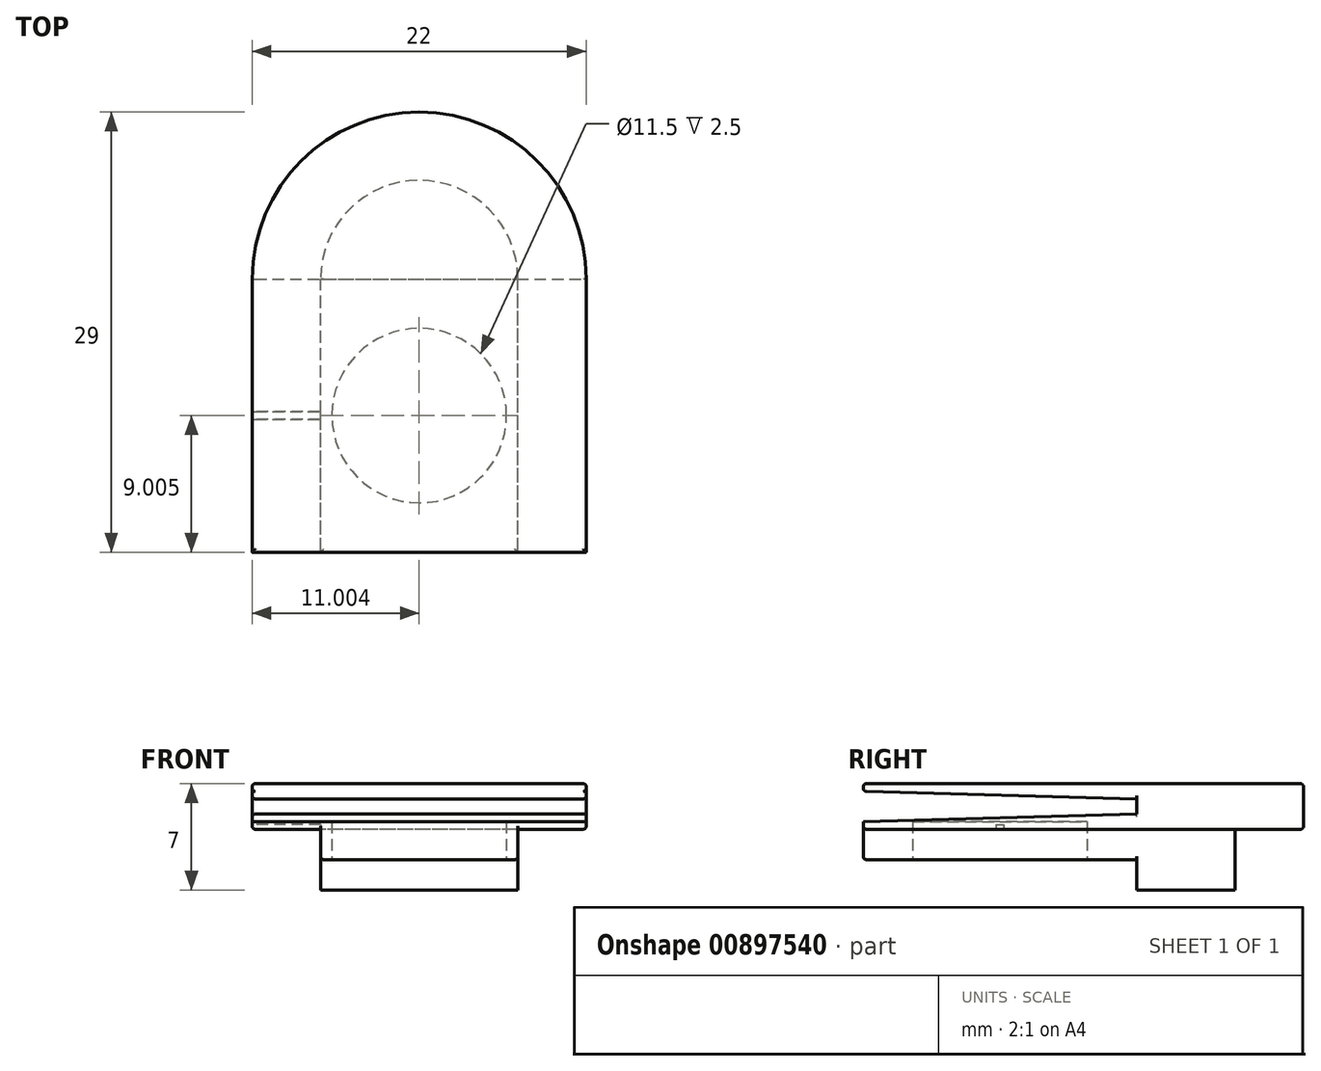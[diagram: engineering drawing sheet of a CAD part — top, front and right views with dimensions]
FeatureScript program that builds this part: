
annotation { "Feature Type Name" : "Feature", "Feature Type Description" : "" }
export const myFeature = defineFeature(function(context is Context, id is Id, definition is map)
    precondition{}
    {
        {
            var Q0;
            Q0=qCreatedBy(makeId("Top.planeOp"),FACE);
            var sketch = newSketch(context, id + "F0", { "sketchPlane" : qUnion([Q0])});
            skArc(sketch, "E0", {"start": v(-33.64, 30.56) * mm, "mid": v(-40.14, 37.06) * mm, "end": v(-46.64, 30.56) * mm});
            skLineSegment(sketch, "E1", {"start": v(-40.14, 30.56) * mm, "end": v(-33.64, 30.56) * mm});
            skLineSegment(sketch, "E2", {"start": v(-33.64, 30.56) * mm, "end": v(-46.64, 30.56) * mm});
            skLineSegment(sketch, "E3", {"start": v(-40.14, 30.56) * mm, "end": v(-40.14, 37.06) * mm, "construction": true});
            skSolve(sketch);
        }
        {
            var Q0;
            Q0 = qSketchRegion(id + "F0", true);
            extrude(context, id + "F1", {"entities" : qUnion([Q0]), "depth" : 13 * mm, "offsetDistance" : 25 * mm});
        }
        {
            var Q0;
            Q0=makeQuery(id+"F1.opExtrude","SWEPT_FACE",FACE,{"disambiguationData":[OSD([sQuery(id+"F0.wireOp",EDGE,"E2")])]});
            var sketch = newSketch(context, id + "F2", { "sketchPlane" : qUnion([Q0])});
            skLineSegment(sketch, "E4.bottom", {"start": v(-46.64, 13) * mm, "end": v(-33.64, 13) * mm});
            skLineSegment(sketch, "E4.top", {"start": v(-46.64, 10) * mm, "end": v(-33.64, 10) * mm});
            skLineSegment(sketch, "E4.left", {"start": v(-46.64, 13) * mm, "end": v(-46.64, 10) * mm});
            skLineSegment(sketch, "E4.right", {"start": v(-33.64, 13) * mm, "end": v(-33.64, 10) * mm});
            skSolve(sketch);
        }
        {
            var Q0;
            Q0 = qSketchRegion(id + "F2", true);
            extrude(context, id + "F3", {"entities" : qUnion([Q0]), "depth" : 18 * mm, "offsetDistance" : 25 * mm});
        }
        {
            var Q0;
            Q0=makeQuery(id+"F3.boolean.opBoolean","MERGE",FACE,{"derivedFrom":[makeQuery(id+"F1.opExtrude","CAP_FACE",FACE,{"disambiguationData":[OSD([sQuery(id+"F0.wireOp",EDGE,"E0"),sQuery(id+"F0.wireOp",EDGE,"E2")])],"isStart":false}),makeQuery(id+"F3.opExtrude","SWEPT_FACE",FACE,{"disambiguationData":[OSD([sQuery(id+"F2.wireOp",EDGE,"E4.bottom")])]})]});
            var sketch = newSketch(context, id + "F4", { "sketchPlane" : qUnion([Q0])});
            skArc(sketch, "E5.0", {"start": v(-29.14, 30.56) * mm, "mid": v(-40.14, 41.56) * mm, "end": v(-51.14, 30.56) * mm});
            skLineSegment(sketch, "E6", {"start": v(-51.14, 30.56) * mm, "end": v(-46.64, 30.56) * mm});
            skLineSegment(sketch, "E7", {"start": v(-29.14, 30.56) * mm, "end": v(-33.64, 30.56) * mm});
            skArc(sketch, "E8.0", {"start": v(-33.64, 30.56) * mm, "mid": v(-40.14, 37.06) * mm, "end": v(-46.64, 30.56) * mm});
            skSolve(sketch);
        }
        {
            var Q0;
            Q0 = qSketchRegion(id + "F4", true);
            extrude(context, id + "F5", {"entities" : qUnion([Q0]), "oppositeDirection" : true, "depth" : 3 * mm, "offsetDistance" : 25 * mm});
        }
        {
            var Q0;
            Q0=makeQuery(id+"F5.opExtrude","SWEPT_FACE",FACE,{"disambiguationData":[OSD([sQuery(id+"F4.wireOp",EDGE,"E6")])]});
            var sketch = newSketch(context, id + "F6", { "sketchPlane" : qUnion([Q0])});
            skLineSegment(sketch, "E9.bottom", {"start": v(-51.14, 10) * mm, "end": v(-46.64, 10) * mm});
            skLineSegment(sketch, "E9.top", {"start": v(-51.14, 13) * mm, "end": v(-46.64, 13) * mm});
            skLineSegment(sketch, "E9.left", {"start": v(-51.14, 10) * mm, "end": v(-51.14, 13) * mm});
            skLineSegment(sketch, "E9.right", {"start": v(-46.64, 10) * mm, "end": v(-46.64, 13) * mm});
            skSolve(sketch);
        }
        {
            var Q0;
            Q0 = qSketchRegion(id + "F6", true);
            extrude(context, id + "F7", {"entities" : qUnion([Q0]), "depth" : 18 * mm, "offsetDistance" : 25 * mm});
        }
        {
            var Q0;
            Q0=makeQuery(id+"F5.opExtrude","SWEPT_FACE",FACE,{"disambiguationData":[OSD([sQuery(id+"F4.wireOp",EDGE,"E7")])]});
            var sketch = newSketch(context, id + "F8", { "sketchPlane" : qUnion([Q0])});
            skLineSegment(sketch, "E10.bottom", {"start": v(-33.64, 13) * mm, "end": v(-29.14, 13) * mm});
            skLineSegment(sketch, "E10.top", {"start": v(-33.64, 10) * mm, "end": v(-29.14, 10) * mm});
            skLineSegment(sketch, "E10.left", {"start": v(-33.64, 13) * mm, "end": v(-33.64, 10) * mm});
            skLineSegment(sketch, "E10.right", {"start": v(-29.14, 13) * mm, "end": v(-29.14, 10) * mm});
            skSolve(sketch);
        }
        {
            var Q0;
            Q0 = qSketchRegion(id + "F8", true);
            extrude(context, id + "F9", {"entities" : qUnion([Q0]), "depth" : 18 * mm, "offsetDistance" : 25 * mm});
        }
        {
            var Q0;
            Q0=makeQuery(id+"F7.opExtrude","SWEPT_FACE",FACE,{"disambiguationData":[OSD([sQuery(id+"F6.wireOp",EDGE,"E9.bottom")])]});
            var sketch = newSketch(context, id + "F10", { "sketchPlane" : qUnion([Q0])});
            skLineSegment(sketch, "E11.bottom", {"start": v(-46.64, -21.31) * mm, "end": v(-51.14, -21.31) * mm});
            skLineSegment(sketch, "E11.top", {"start": v(-46.64, -21.81) * mm, "end": v(-51.14, -21.81) * mm});
            skLineSegment(sketch, "E11.left", {"start": v(-46.64, -21.31) * mm, "end": v(-46.64, -21.81) * mm});
            skLineSegment(sketch, "E11.right", {"start": v(-51.14, -21.31) * mm, "end": v(-51.14, -21.81) * mm});
            skPoint(sketch, "E11.middle", {"position": v(-48.89, -21.56) * mm});
            skPoint(sketch, "E11.middle.positionSnap0", {"position": v(-51.14, -21.56) * mm});
            skPoint(sketch, "E11.middle.positionSnap1", {"position": v(-48.89, -30.56) * mm});
            skPoint(sketch, "E11.centerSnap0", {"position": v(-51.14, -21.56) * mm});
            skPoint(sketch, "E11.centerSnap1", {"position": v(-48.89, -30.56) * mm});
            skSolve(sketch);
        }
        {
            var Q0;
            Q0 = qSketchRegion(id + "F10", true);
            extrude(context, id + "F11", {"entities" : qUnion([Q0]), "depth" : 0.5 * mm, "offsetDistance" : 25 * mm});
        }
        {
            var Q0;
            Q0=makeQuery(id+"F11.opExtrude","CAP_FACE",FACE,{"disambiguationData":[OSD([sQuery(id+"F10.wireOp",EDGE,"E11.bottom"),sQuery(id+"F10.wireOp",EDGE,"E11.top"),sQuery(id+"F10.wireOp",EDGE,"E11.left"),sQuery(id+"F10.wireOp",EDGE,"E11.right")])],"isStart":false});
            var sketch = newSketch(context, id + "F12", { "sketchPlane" : qUnion([Q0])});
            skLineSegment(sketch, "E12.bottom", {"start": v(-51.14, -21.81) * mm, "end": v(-46.64, -21.81) * mm});
            skLineSegment(sketch, "E12.top", {"start": v(-51.14, -21.31) * mm, "end": v(-46.64, -21.31) * mm});
            skLineSegment(sketch, "E12.left", {"start": v(-51.14, -21.81) * mm, "end": v(-51.14, -21.31) * mm});
            skLineSegment(sketch, "E12.right", {"start": v(-46.64, -21.81) * mm, "end": v(-46.64, -21.31) * mm});
            skSolve(sketch);
        }
        {
            var Q0;
            Q0 = qSketchRegion(id + "F12", true);
            extrude(context, id + "F13", {"entities" : qUnion([Q0]), "operationType" : NewBodyOperationType.REMOVE, "oppositeDirection" : true, "depth" : 0.8 * mm, "offsetDistance" : 25 * mm});
        }
        {
            var Q0;
            Q0=makeQuery(id+"F1.opExtrude","CAP_FACE",FACE,{"disambiguationData":[OSD([sQuery(id+"F0.wireOp",EDGE,"E0"),sQuery(id+"F0.wireOp",EDGE,"E2")])],"isStart":true});
            var sketch = newSketch(context, id + "F14", { "sketchPlane" : qUnion([Q0])});
            skArc(sketch, "E13", {"start": v(-46.64, -30.56) * mm, "mid": v(-40.14, -37.06) * mm, "end": v(-33.64, -30.56) * mm});
            skLineSegment(sketch, "E14", {"start": v(-46.64, -30.56) * mm, "end": v(-33.64, -30.56) * mm});
            skSolve(sketch);
        }
        {
            var Q0;
            Q0 = qSketchRegion(id + "F14", true);
            extrude(context, id + "F15", {"entities" : qUnion([Q0]), "operationType" : NewBodyOperationType.REMOVE, "oppositeDirection" : true, "depth" : 6 * mm, "offsetDistance" : 25 * mm});
        }
        {
            var Q0;
            Q0=makeQuery(id+"F3.opExtrude","SWEPT_FACE",FACE,{"disambiguationData":[OSD([sQuery(id+"F2.wireOp",EDGE,"E4.top")])]});
            var sketch = newSketch(context, id + "F16", { "sketchPlane" : qUnion([Q0])});
            skLineSegment(sketch, "E15.bottom", {"start": v(-33.64, -30.56) * mm, "end": v(-46.64, -30.56) * mm});
            skLineSegment(sketch, "E15.top", {"start": v(-33.64, -12.56) * mm, "end": v(-46.64, -12.56) * mm});
            skLineSegment(sketch, "E15.left", {"start": v(-33.64, -30.56) * mm, "end": v(-33.64, -12.56) * mm});
            skLineSegment(sketch, "E15.right", {"start": v(-46.64, -30.56) * mm, "end": v(-46.64, -12.56) * mm});
            skSolve(sketch);
        }
        {
            var Q0;
            Q0 = qSketchRegion(id + "F16", true);
            extrude(context, id + "F17", {"entities" : qUnion([Q0]), "operationType" : NewBodyOperationType.ADD, "depth" : 2 * mm, "offsetDistance" : 25 * mm});
        }
        {
            var Q0;
            Q0=makeQuery(id+"F17.opExtrude","CAP_FACE",FACE,{"disambiguationData":[OSD([sQuery(id+"F16.wireOp",EDGE,"E15.bottom"),sQuery(id+"F16.wireOp",EDGE,"E15.top"),sQuery(id+"F16.wireOp",EDGE,"E15.left"),sQuery(id+"F16.wireOp",EDGE,"E15.right")])],"isStart":false});
            var sketch = newSketch(context, id + "F18", { "sketchPlane" : qUnion([Q0])});
            skCircle(sketch, "E16", {"center": v(-40.14, -21.56) * mm, "radius": 5.75 * mm});
            skPoint(sketch, "E16.centerSnap0", {"position": v(-46.64, -21.56) * mm});
            skPoint(sketch, "E16.centerSnap1", {"position": v(-40.14, -30.56) * mm});
            skSolve(sketch);
        }
        {
            var Q0;
            Q0 = qSketchRegion(id + "F18", true);
            extrude(context, id + "F19", {"entities" : qUnion([Q0]), "operationType" : NewBodyOperationType.REMOVE, "oppositeDirection" : true, "depth" : 2.5 * mm, "offsetDistance" : 25 * mm});
        }
        {
            var Q0;
            Q0=makeQuery(id+"F9.opExtrude","SWEPT_FACE",FACE,{"disambiguationData":[OSD([sQuery(id+"F8.wireOp",EDGE,"E10.right")])]});
            var sketch = newSketch(context, id + "F20", { "sketchPlane" : qUnion([Q0])});
            skLineSegment(sketch, "E17", {"start": v(30.56, 11) * mm, "end": v(30.56, 12) * mm});
            skLineSegment(sketch, "E18", {"start": v(30.56, 12) * mm, "end": v(12.56, 12.5) * mm});
            skLineSegment(sketch, "E19", {"start": v(12.56, 12.5) * mm, "end": v(12.56, 10.5) * mm});
            skLineSegment(sketch, "E20", {"start": v(12.56, 10.5) * mm, "end": v(30.56, 11) * mm});
            skSolve(sketch);
        }
        {
            var Q0;
            Q0 = qSketchRegion(id + "F20", true);
            extrude(context, id + "F21", {"entities" : qUnion([Q0]), "operationType" : NewBodyOperationType.REMOVE, "endBound" : BoundingType.THROUGH_ALL, "oppositeDirection" : true, "depth" : 24.1 * mm, "offsetDistance" : 25 * mm});
        }
        {
            var Q0;
            Q0=makeQuery(id+"F15.boolean.opBoolean","COPY",EDGE,{"derivedFrom":makeQuery(id+"F15.opExtrude","CAP_EDGE",EDGE,{"disambiguationData":[OSD([sQuery(id+"F14.wireOp",EDGE,"E14")])],"isStart":false})});
            var Q1;
            Q1=makeQuery(id+"F15.boolean.opBoolean","COPY",EDGE,{"derivedFrom":makeQuery(id+"F15.opExtrude","CAP_EDGE",EDGE,{"disambiguationData":[OSD([sQuery(id+"F14.wireOp",EDGE,"E13")])],"isStart":false})});
            var Q2;
            Q2=makeQuery(id+"F5.opExtrude","CAP_EDGE",EDGE,{"disambiguationData":[OSD([sQuery(id+"F4.wireOp",EDGE,"E5.0")])],"isStart":false});
            var Q3;
            Q3=makeQuery(id+"F17.opExtrude","CAP_EDGE",EDGE,{"disambiguationData":[OSD([sQuery(id+"F16.wireOp",EDGE,"E15.right")])],"isStart":false});
            var Q4;
            Q4=makeQuery(id+"F17.opExtrude","CAP_EDGE",EDGE,{"disambiguationData":[OSD([sQuery(id+"F16.wireOp",EDGE,"E15.left")])],"isStart":false});
            var Q5;
            Q5=makeQuery(id+"F17.opExtrude","CAP_EDGE",EDGE,{"disambiguationData":[OSD([sQuery(id+"F16.wireOp",EDGE,"E15.top")])],"isStart":false});
            var Q6;
            {var subQ0=sQuery(id+"F20.wireOp",EDGE,"E20");Q6=makeQuery(id+"F21.boolean.opBoolean","COPY",EDGE,{"disambiguationData":[topologyDisambiguationEdgeConnected([makeQuery(id+"F17.opExtrude","SWEPT_FACE",FACE,{"disambiguationData":[OSD([sQuery(id+"F16.wireOp",EDGE,"E15.top")])]})])],"derivedFrom":makeQuery(id+"F21.opExtrude","SWEPT_EDGE",EDGE,{"disambiguationData":[OSD([sQuery(id+"F8.wireOp",EDGE,"E10.right"),sQuery(id+"F20.wireOp",EDGE,"E19"),subQ0])]})});}
            var Q7;
            {var subQ0=sQuery(id+"F20.wireOp",EDGE,"E20");Q7=makeQuery(id+"F21.boolean.opBoolean","COPY",EDGE,{"disambiguationData":[topologyDisambiguationEdgeConnected([makeQuery(id+"F7.opExtrude","CAP_FACE",FACE,{"disambiguationData":[OSD([sQuery(id+"F6.wireOp",EDGE,"E9.bottom"),sQuery(id+"F6.wireOp",EDGE,"E9.top"),sQuery(id+"F6.wireOp",EDGE,"E9.left"),sQuery(id+"F6.wireOp",EDGE,"E9.right")])],"isStart":false})])],"derivedFrom":makeQuery(id+"F21.opExtrude","SWEPT_EDGE",EDGE,{"disambiguationData":[OSD([sQuery(id+"F8.wireOp",EDGE,"E10.right"),sQuery(id+"F20.wireOp",EDGE,"E19"),subQ0])]})});}
            var Q8;
            {var subQ0=sQuery(id+"F8.wireOp",EDGE,"E10.right");var subQ1=sQuery(id+"F20.wireOp",EDGE,"E20");Q8=makeQuery(id+"F21.boolean.opBoolean","COPY",EDGE,{"disambiguationData":[topologyDisambiguationEdgeConnected([makeQuery(id+"F9.opExtrude","CAP_FACE",FACE,{"disambiguationData":[OSD([sQuery(id+"F8.wireOp",EDGE,"E10.bottom"),sQuery(id+"F8.wireOp",EDGE,"E10.top"),sQuery(id+"F8.wireOp",EDGE,"E10.left"),subQ0])],"isStart":false})])],"derivedFrom":makeQuery(id+"F21.opExtrude","SWEPT_EDGE",EDGE,{"disambiguationData":[OSD([subQ0,sQuery(id+"F20.wireOp",EDGE,"E19"),subQ1])]})});}
            var Q9;
            Q9=makeQuery(id+"F9.opExtrude","CAP_EDGE",EDGE,{"disambiguationData":[OSD([sQuery(id+"F8.wireOp",EDGE,"E10.top")])],"isStart":false});
            var Q10;
            Q10=makeQuery(id+"F7.opExtrude","CAP_EDGE",EDGE,{"disambiguationData":[OSD([sQuery(id+"F6.wireOp",EDGE,"E9.bottom")])],"isStart":false});
            var Q11;
            {var subQ0=sQuery(id+"F16.wireOp",EDGE,"E15.right");var subQ1=sQuery(id+"F16.wireOp",EDGE,"E15.top");var subQ2=sQuery(id+"F2.wireOp",EDGE,"E4.left");Q11=makeQuery(id+"F21.boolean.opBoolean","SPLIT",EDGE,{"disambiguationData":[TD([makeQuery(id+"F21.opExtrude","SWEPT_FACE",FACE,{"disambiguationData":[OSD([sQuery(id+"F20.wireOp",EDGE,"E20")])]})])],"derivedFrom":makeQuery(id+"F17.boolean.opBoolean","MERGE",EDGE,{"derivedFrom":[makeQuery(id+"F3.opExtrude","CAP_EDGE",EDGE,{"disambiguationData":[OSD([subQ2])],"isStart":false}),makeQuery(id+"F17.opExtrude","SWEPT_EDGE",EDGE,{"disambiguationData":[OSD([subQ1,subQ0])]})]})});}
            var Q12;
            {var subQ0=sQuery(id+"F16.wireOp",EDGE,"E15.left");var subQ1=sQuery(id+"F16.wireOp",EDGE,"E15.top");var subQ2=sQuery(id+"F2.wireOp",EDGE,"E4.right");Q12=makeQuery(id+"F21.boolean.opBoolean","SPLIT",EDGE,{"disambiguationData":[TD([makeQuery(id+"F21.opExtrude","SWEPT_FACE",FACE,{"disambiguationData":[OSD([sQuery(id+"F20.wireOp",EDGE,"E20")])]})])],"derivedFrom":makeQuery(id+"F17.boolean.opBoolean","MERGE",EDGE,{"derivedFrom":[makeQuery(id+"F3.opExtrude","CAP_EDGE",EDGE,{"disambiguationData":[OSD([subQ2])],"isStart":false}),makeQuery(id+"F17.opExtrude","SWEPT_EDGE",EDGE,{"disambiguationData":[OSD([subQ1,subQ0])]})]})});}
            var Q13;
            {var subQ0=sQuery(id+"F20.wireOp",EDGE,"E18");Q13=makeQuery(id+"F21.boolean.opBoolean","COPY",EDGE,{"disambiguationData":[topologyDisambiguationEdgeConnected([makeQuery(id+"F17.opExtrude","SWEPT_FACE",FACE,{"disambiguationData":[OSD([sQuery(id+"F16.wireOp",EDGE,"E15.top")])]})])],"derivedFrom":makeQuery(id+"F21.opExtrude","SWEPT_EDGE",EDGE,{"disambiguationData":[OSD([sQuery(id+"F8.wireOp",EDGE,"E10.right"),subQ0,sQuery(id+"F20.wireOp",EDGE,"E19")])]})});}
            var Q14;
            {var subQ0=sQuery(id+"F20.wireOp",EDGE,"E18");Q14=makeQuery(id+"F21.boolean.opBoolean","COPY",EDGE,{"disambiguationData":[topologyDisambiguationEdgeConnected([makeQuery(id+"F7.opExtrude","CAP_FACE",FACE,{"disambiguationData":[OSD([sQuery(id+"F6.wireOp",EDGE,"E9.bottom"),sQuery(id+"F6.wireOp",EDGE,"E9.top"),sQuery(id+"F6.wireOp",EDGE,"E9.left"),sQuery(id+"F6.wireOp",EDGE,"E9.right")])],"isStart":false})])],"derivedFrom":makeQuery(id+"F21.opExtrude","SWEPT_EDGE",EDGE,{"disambiguationData":[OSD([sQuery(id+"F8.wireOp",EDGE,"E10.right"),subQ0,sQuery(id+"F20.wireOp",EDGE,"E19")])]})});}
            var Q15;
            {var subQ0=sQuery(id+"F8.wireOp",EDGE,"E10.right");var subQ1=sQuery(id+"F20.wireOp",EDGE,"E18");Q15=makeQuery(id+"F21.boolean.opBoolean","COPY",EDGE,{"disambiguationData":[topologyDisambiguationEdgeConnected([makeQuery(id+"F9.opExtrude","CAP_FACE",FACE,{"disambiguationData":[OSD([sQuery(id+"F8.wireOp",EDGE,"E10.bottom"),sQuery(id+"F8.wireOp",EDGE,"E10.top"),sQuery(id+"F8.wireOp",EDGE,"E10.left"),subQ0])],"isStart":false})])],"derivedFrom":makeQuery(id+"F21.opExtrude","SWEPT_EDGE",EDGE,{"disambiguationData":[OSD([subQ0,subQ1,sQuery(id+"F20.wireOp",EDGE,"E19")])]})});}
            var Q16;
            Q16=makeQuery(id+"F9.opExtrude","CAP_EDGE",EDGE,{"disambiguationData":[OSD([sQuery(id+"F8.wireOp",EDGE,"E10.bottom")])],"isStart":false});
            var Q17;
            Q17=makeQuery(id+"F3.opExtrude","CAP_EDGE",EDGE,{"disambiguationData":[OSD([sQuery(id+"F2.wireOp",EDGE,"E4.bottom")])],"isStart":false});
            var Q18;
            Q18=makeQuery(id+"F7.opExtrude","CAP_EDGE",EDGE,{"disambiguationData":[OSD([sQuery(id+"F6.wireOp",EDGE,"E9.top")])],"isStart":false});
            var Q19;
            Q19=makeQuery(id+"F21.boolean.opBoolean","INTERSECT",EDGE,{"derivedFrom":[makeQuery(id+"F7.opExtrude","SWEPT_FACE",FACE,{"disambiguationData":[OSD([sQuery(id+"F6.wireOp",EDGE,"E9.left")])]}),makeQuery(id+"F21.opExtrude","SWEPT_FACE",FACE,{"disambiguationData":[OSD([sQuery(id+"F20.wireOp",EDGE,"E18")])]})]});
            var Q20;
            Q20=makeQuery(id+"F7.opExtrude","SWEPT_EDGE",EDGE,{"disambiguationData":[OSD([sQuery(id+"F6.wireOp",EDGE,"E9.top"),sQuery(id+"F6.wireOp",EDGE,"E9.left")])]});
            var Q21;
            {var subQ0=sQuery(id+"F6.wireOp",EDGE,"E9.bottom");var subQ1=sQuery(id+"F6.wireOp",EDGE,"E9.left");Q21=makeQuery(id+"F13.boolean.opBoolean","SPLIT",EDGE,{"disambiguationData":[TD([makeQuery(id+"F13.opExtrude","SWEPT_FACE",FACE,{"disambiguationData":[OSD([sQuery(id+"F12.wireOp",EDGE,"E12.top")])]})])],"derivedFrom":makeQuery(id+"F7.opExtrude","SWEPT_EDGE",EDGE,{"disambiguationData":[OSD([subQ0,subQ1])]})});}
            var Q22;
            Q22=makeQuery(id+"F21.boolean.opBoolean","INTERSECT",EDGE,{"derivedFrom":[makeQuery(id+"F7.opExtrude","SWEPT_FACE",FACE,{"disambiguationData":[OSD([sQuery(id+"F6.wireOp",EDGE,"E9.left")])]}),makeQuery(id+"F21.opExtrude","SWEPT_FACE",FACE,{"disambiguationData":[OSD([sQuery(id+"F20.wireOp",EDGE,"E20")])]})]});
            var Q23;
            {var subQ0=sQuery(id+"F6.wireOp",EDGE,"E9.bottom");var subQ1=sQuery(id+"F6.wireOp",EDGE,"E9.left");Q23=makeQuery(id+"F13.boolean.opBoolean","SPLIT",EDGE,{"disambiguationData":[TD([makeQuery(id+"F13.opExtrude","SWEPT_FACE",FACE,{"disambiguationData":[OSD([sQuery(id+"F12.wireOp",EDGE,"E12.bottom")])]})])],"derivedFrom":makeQuery(id+"F7.opExtrude","SWEPT_EDGE",EDGE,{"disambiguationData":[OSD([subQ0,subQ1])]})});}
            var Q24;
            Q24=makeQuery(id+"F5.opExtrude","CAP_EDGE",EDGE,{"disambiguationData":[OSD([sQuery(id+"F4.wireOp",EDGE,"E5.0")])],"isStart":true});
            var Q25;
            Q25=makeQuery(id+"F21.boolean.opBoolean","COPY",EDGE,{"derivedFrom":makeQuery(id+"F21.opExtrude","CAP_EDGE",EDGE,{"disambiguationData":[OSD([sQuery(id+"F20.wireOp",EDGE,"E20")])],"isStart":true})});
            var Q26;
            Q26=makeQuery(id+"F9.opExtrude","SWEPT_EDGE",EDGE,{"disambiguationData":[OSD([sQuery(id+"F8.wireOp",EDGE,"E10.top"),sQuery(id+"F8.wireOp",EDGE,"E10.right")])]});
            var Q27;
            Q27=makeQuery(id+"F9.opExtrude","SWEPT_EDGE",EDGE,{"disambiguationData":[OSD([sQuery(id+"F8.wireOp",EDGE,"E10.bottom"),sQuery(id+"F8.wireOp",EDGE,"E10.right")])]});
            var Q28;
            Q28=makeQuery(id+"F21.boolean.opBoolean","COPY",EDGE,{"derivedFrom":makeQuery(id+"F21.opExtrude","CAP_EDGE",EDGE,{"disambiguationData":[OSD([sQuery(id+"F20.wireOp",EDGE,"E18")])],"isStart":true})});
            var Q29;
            Q29=makeQuery(id+"F5.opExtrude","CAP_EDGE",EDGE,{"disambiguationData":[OSD([sQuery(id+"F4.wireOp",EDGE,"E8.0")])],"isStart":false});
            var Q30;
            {var subQ0=sQuery(id+"F6.wireOp",EDGE,"E9.bottom");var subQ1=sQuery(id+"F6.wireOp",EDGE,"E9.right");Q30=makeQuery(id+"F13.boolean.opBoolean","SPLIT",EDGE,{"disambiguationData":[TD([makeQuery(id+"F13.opExtrude","SWEPT_FACE",FACE,{"disambiguationData":[OSD([sQuery(id+"F12.wireOp",EDGE,"E12.bottom")])]})])],"derivedFrom":makeQuery(id+"F7.opExtrude","SWEPT_EDGE",EDGE,{"disambiguationData":[OSD([subQ0,subQ1])]})});}
            var Q31;
            {var subQ0=sQuery(id+"F6.wireOp",EDGE,"E9.bottom");var subQ1=sQuery(id+"F6.wireOp",EDGE,"E9.right");Q31=makeQuery(id+"F13.boolean.opBoolean","SPLIT",EDGE,{"disambiguationData":[TD([makeQuery(id+"F13.opExtrude","SWEPT_FACE",FACE,{"disambiguationData":[OSD([sQuery(id+"F12.wireOp",EDGE,"E12.top")])]})])],"derivedFrom":makeQuery(id+"F7.opExtrude","SWEPT_EDGE",EDGE,{"disambiguationData":[OSD([subQ0,subQ1])]})});}
            var Q32;
            Q32=makeQuery(id+"F9.opExtrude","SWEPT_EDGE",EDGE,{"disambiguationData":[OSD([sQuery(id+"F8.wireOp",EDGE,"E10.top"),sQuery(id+"F8.wireOp",EDGE,"E10.left")])]});
            fillet(context, id + "F22", {"entities" : qUnion([Q0, Q1, Q2, Q3, Q4, Q5, Q6, Q7, Q8, Q9, Q10, Q11, Q12, Q13, Q14, Q15, Q16, Q17, Q18, Q19, Q20, Q21, Q22, Q23, Q24, Q25, Q26, Q27, Q28, Q29, Q30, Q31, Q32]), "radius" : 0.2 * mm, "tangentPropagation" : true, "allowEdgeOverflow" : false});
        }
    });
